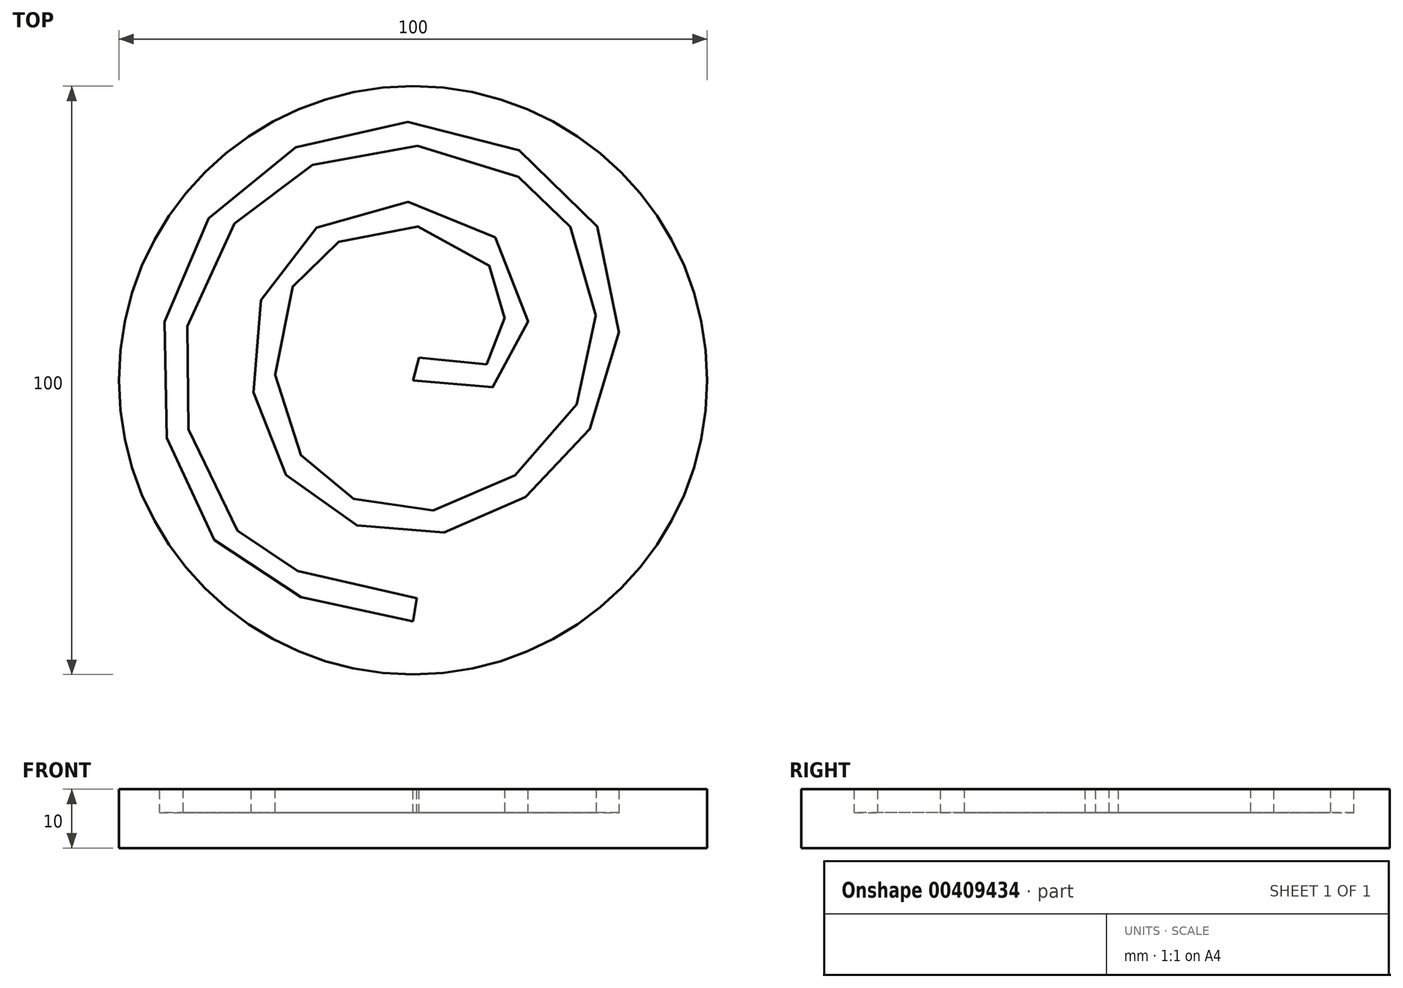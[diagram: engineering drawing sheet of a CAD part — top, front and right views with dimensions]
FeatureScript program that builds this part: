
annotation { "Feature Type Name" : "Feature", "Feature Type Description" : "" }
export const myFeature = defineFeature(function(context is Context, id is Id, definition is map)
    precondition{}
    {
        {
            var Q0;
            Q0=qCreatedBy(makeId("Top.planeOp"),FACE);
            var sketch = newSketch(context, id + "F0", { "sketchPlane" : qUnion([Q0])});
            skCircle(sketch, "E0", {"center": v(0, 0) * mm, "radius": 50 * mm});
            skSolve(sketch);
        }
        {
            var Q0;
            Q0 = qSketchRegion(id + "F0", true);
            extrude(context, id + "F1", {"entities" : qUnion([Q0]), "depth" : 10 * mm, "offsetDistance" : 25 * mm});
        }
        {
            var Q0;
            Q0=makeQuery(id+"F1.opExtrude","CAP_FACE",FACE,{"disambiguationData":[OSD([sQuery(id+"F0.wireOp",EDGE,"E0")])],"isStart":false});
            var sketch = newSketch(context, id + "F2", { "sketchPlane" : qUnion([Q0])});
            skLineSegment(sketch, "E1", {"start": v(0, 0) * mm, "end": v(42.94, 42.94) * mm, "construction": true});
            skLineSegment(sketch, "E2", {"start": v(0, 0) * mm, "end": v(61.83, -61.83) * mm, "construction": true});
            skLineSegment(sketch, "E3", {"start": v(0, 0) * mm, "end": v(-49.98, -49.98) * mm, "construction": true});
            skLineSegment(sketch, "E4", {"start": v(0, 0) * mm, "end": v(-42.94, 42.94) * mm, "construction": true});
            skFitSpline(sketch, "E5", {"points": [v(0, 0) * mm, v(15.6, 0) * mm, v(18.21, 18.21) * mm, v(0, 30.25) * mm, v(-21.47, 21.47) * mm, v(-27.35, 0) * mm, v(-18.98, -18.98) * mm, v(0, -26.32) * mm, v(19.52, -19.52) * mm, v(33.68, 0) * mm, v(29.35, 29.35) * mm, v(0, 43.87) * mm, v(-31.42, 31.42) * mm, v(-43.07, 0) * mm, v(-30.5, -30.5) * mm, v(0, -40.99) * mm], "startDerivative": vector(353.86, -89.71) * mm, "endDerivative": vector(466.28, -76.18) * mm});
            skFitSpline(sketch, "E6.0", {"points": [v(0.98, 3.88) * mm, v(1.9, 3.64) * mm, v(3.7, 3.2) * mm, v(5.76, 2.73) * mm, v(7.28, 2.47) * mm, v(8.34, 2.32) * mm, v(9.32, 2.25) * mm, v(10.19, 2.23) * mm, v(10.95, 2.28) * mm, v(11.59, 2.39) * mm, v(12.02, 2.51) * mm, v(12.32, 2.63) * mm, v(12.52, 2.72) * mm, v(12.7, 2.83) * mm, v(12.85, 2.93) * mm, v(12.95, 3) * mm, v(13, 3.05) * mm, v(13.07, 3.1) * mm, v(13.14, 3.15) * mm, v(13.25, 3.27) * mm, v(13.4, 3.43) * mm, v(13.6, 3.66) * mm, v(13.8, 3.92) * mm, v(14.05, 4.32) * mm, v(14.37, 4.91) * mm, v(14.72, 5.74) * mm, v(15.02, 6.67) * mm, v(15.27, 7.69) * mm, v(15.45, 8.77) * mm, v(15.56, 9.9) * mm, v(15.59, 11.06) * mm, v(15.54, 12.23) * mm, v(15.41, 13.4) * mm, v(15.24, 14.34) * mm, v(15.06, 15.07) * mm, v(14.9, 15.61) * mm, v(14.76, 16.05) * mm, v(14.64, 16.39) * mm, v(14.54, 16.64) * mm, v(14.44, 16.88) * mm, v(14.3, 17.21) * mm, v(14.1, 17.61) * mm, v(13.85, 18.08) * mm, v(13.48, 18.7) * mm, v(12.98, 19.45) * mm, v(12.3, 20.3) * mm, v(11.54, 21.11) * mm, v(10.43, 22.13) * mm, v(8.87, 23.29) * mm, v(6.78, 24.45) * mm, v(4.9, 25.2) * mm, v(3.32, 25.67) * mm, v(2.12, 25.95) * mm, v(1.1, 26.12) * mm, v(0.28, 26.22) * mm, v(-0.33, 26.27) * mm, v(-0.94, 26.3) * mm, v(-1.77, 26.33) * mm, v(-2.8, 26.31) * mm, v(-4.06, 26.22) * mm, v(-5.72, 26) * mm, v(-7.78, 25.54) * mm, v(-10.18, 24.73) * mm, v(-12.46, 23.67) * mm, v(-14.22, 22.6) * mm, v(-15.54, 21.64) * mm, v(-16.46, 20.88) * mm, v(-17.19, 20.2) * mm, v(-17.74, 19.65) * mm, v(-18.06, 19.3) * mm, v(-18.32, 19) * mm, v(-18.57, 18.7) * mm, v(-18.87, 18.33) * mm, v(-19.22, 17.87) * mm, v(-19.66, 17.24) * mm, v(-20.18, 16.43) * mm, v(-20.75, 15.4) * mm, v(-21.27, 14.34) * mm, v(-21.88, 12.87) * mm, v(-22.52, 10.95) * mm, v(-23.06, 8.52) * mm, v(-23.4, 6.02) * mm, v(-23.5, 3.9) * mm, v(-23.48, 2.19) * mm, v(-23.42, 0.91) * mm, v(-23.3, -0.36) * mm, v(-23.15, -1.6) * mm, v(-22.94, -2.85) * mm, v(-22.61, -4.47) * mm, v(-22.08, -6.43) * mm, v(-21.25, -8.68) * mm, v(-20.42, -10.43) * mm, v(-19.67, -11.76) * mm, v(-19.06, -12.72) * mm, v(-18.4, -13.64) * mm, v(-17.71, -14.5) * mm, v(-17.1, -15.2) * mm, v(-16.59, -15.72) * mm, v(-16.2, -16.1) * mm, v(-15.79, -16.48) * mm, v(-15.23, -16.97) * mm, v(-14.5, -17.55) * mm, v(-13.58, -18.2) * mm, v(-12.3, -19.03) * mm, v(-10.59, -19.94) * mm, v(-8.42, -20.84) * mm, v(-6.16, -21.54) * mm, v(-4.23, -21.95) * mm, v(-2.68, -22.17) * mm, v(-1.52, -22.27) * mm, v(-0.55, -22.32) * mm, v(0.22, -22.32) * mm, v(0.98, -22.3) * mm, v(1.94, -22.26) * mm, v(3.46, -22.1) * mm, v(5.36, -21.79) * mm, v(7.62, -21.2) * mm, v(9.85, -20.4) * mm, v(12.06, -19.41) * mm, v(13.86, -18.44) * mm, v(15.28, -17.57) * mm, v(16.16, -17) * mm, v(16.86, -16.51) * mm, v(17.55, -16.02) * mm, v(18.4, -15.37) * mm, v(19.4, -14.56) * mm, v(20.69, -13.44) * mm, v(22.24, -11.94) * mm, v(23.97, -10) * mm, v(25.54, -7.94) * mm, v(26.96, -5.74) * mm, v(27.98, -3.8) * mm, v(28.7, -2.16) * mm, v(29.2, -0.9) * mm, v(29.63, 0.38) * mm, v(30, 1.7) * mm, v(30.33, 3.07) * mm, v(30.69, 4.94) * mm, v(30.98, 7.35) * mm, v(31.09, 10.3) * mm, v(30.94, 13.29) * mm, v(30.52, 16.25) * mm, v(29.96, 18.65) * mm, v(29.37, 20.52) * mm, v(28.86, 21.9) * mm, v(28.28, 23.23) * mm, v(27.64, 24.52) * mm, v(27.05, 25.55) * mm, v(26.54, 26.36) * mm, v(26.21, 26.85) * mm, v(25.94, 27.23) * mm, v(25.66, 27.62) * mm, v(25.3, 28.1) * mm, v(24.85, 28.65) * mm, v(24.22, 29.37) * mm, v(23.4, 30.26) * mm, v(22.33, 31.27) * mm, v(21.2, 32.24) * mm, v(19.61, 33.46) * mm, v(17.48, 34.87) * mm, v(14.73, 36.34) * mm, v(11.8, 37.57) * mm, v(8.75, 38.56) * mm, v(6.13, 39.17) * mm, v(4, 39.52) * mm, v(2.4, 39.72) * mm, v(0.8, 39.85) * mm, v(-0.81, 39.9) * mm, v(-2.42, 39.9) * mm, v(-4.56, 39.79) * mm, v(-7.23, 39.48) * mm, v(-10.38, 38.86) * mm, v(-13.47, 37.98) * mm, v(-16.47, 36.85) * mm, v(-19.35, 35.5) * mm, v(-22.1, 33.92) * mm, v(-24.24, 32.43) * mm, v(-25.87, 31.14) * mm, v(-27.03, 30.12) * mm, v(-28.15, 29.06) * mm, v(-29.21, 27.95) * mm, v(-30.22, 26.8) * mm, v(-31.5, 25.2) * mm, v(-32.97, 23.08) * mm, v(-34.52, 20.39) * mm, v(-35.86, 17.55) * mm, v(-36.97, 14.6) * mm, v(-37.85, 11.53) * mm, v(-38.5, 8.38) * mm, v(-38.93, 5.16) * mm, v(-39.08, 2.44) * mm, v(-39.08, 0.24) * mm, v(-39.02, -1.4) * mm, v(-38.9, -3.06) * mm, v(-38.66, -5.25) * mm, v(-38.2, -7.98) * mm, v(-37.44, -11.19) * mm, v(-36.45, -14.29) * mm, v(-35.25, -17.25) * mm, v(-33.84, -20.02) * mm, v(-32.25, -22.58) * mm, v(-30.77, -24.51) * mm, v(-29.67, -25.74) * mm, v(-29.03, -26.4) * mm, v(-28.53, -26.9) * mm, v(-28.11, -27.28) * mm, v(-27.77, -27.58) * mm, v(-27.26, -28.02) * mm, v(-26.46, -28.65) * mm, v(-25.34, -29.43) * mm, v(-24.18, -30.16) * mm, v(-22.96, -30.84) * mm, v(-21.27, -31.68) * mm, v(-19.03, -32.63) * mm, v(-16.14, -33.6) * mm, v(-13.07, -34.45) * mm, v(-9.84, -35.19) * mm, v(-5.34, -36.06) * mm, v(-1.78, -36.64) * mm, v(0.65, -37.04) * mm]});
            skLineSegment(sketch, "E7", {"start": v(0, 0) * mm, "end": v(0.98, 3.88) * mm});
            skLineSegment(sketch, "E8", {"start": v(0, -40.99) * mm, "end": v(0.65, -37.04) * mm});
            skSolve(sketch);
        }
        {
            var Q0;
            Q0 = qSketchRegion(id + "F2", true);
            extrude(context, id + "F3", {"entities" : qUnion([Q0]), "operationType" : NewBodyOperationType.REMOVE, "oppositeDirection" : true, "depth" : 4 * mm, "offsetDistance" : 25 * mm});
        }
    });
